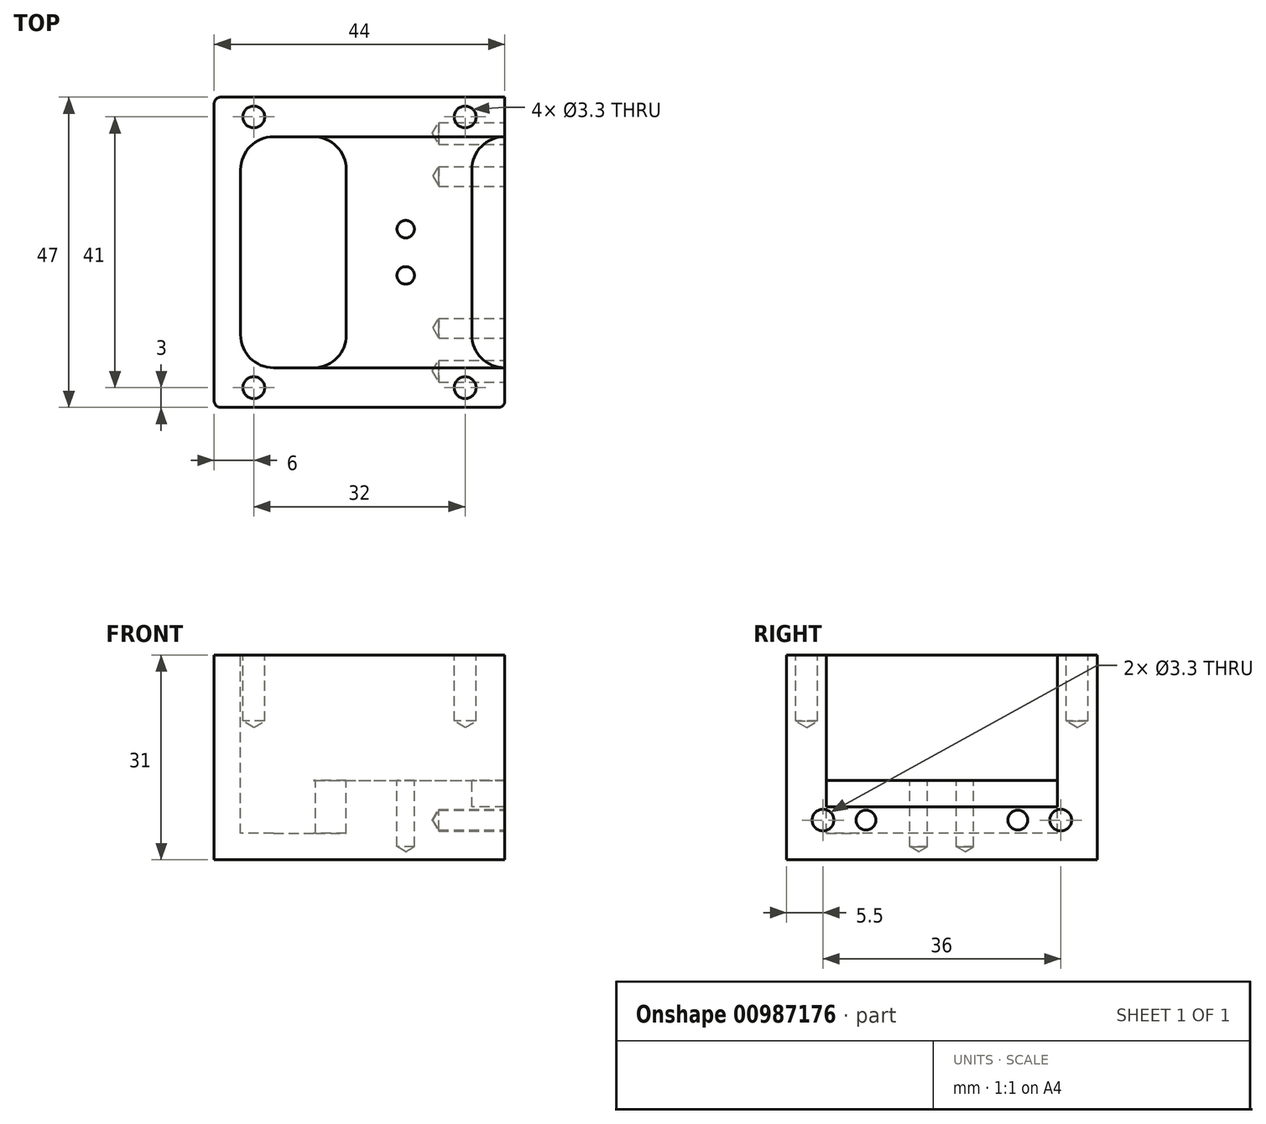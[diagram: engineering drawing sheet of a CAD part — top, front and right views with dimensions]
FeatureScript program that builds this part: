
annotation { "Feature Type Name" : "Feature", "Feature Type Description" : "" }
export const myFeature = defineFeature(function(context is Context, id is Id, definition is map)
    precondition{}
    {
        {
            var Q0;
            Q0=qCreatedBy(makeId("Top.planeOp"),FACE);
            var sketch = newSketch(context, id + "F0", { "sketchPlane" : qUnion([Q0])});
            skLineSegment(sketch, "E0", {"start": v(0, -28.75) * mm, "end": v(-27, -28.75) * mm});
            skLineSegment(sketch, "E1.bottom", {"start": v(-27, -28.75) * mm, "end": v(17, -28.75) * mm});
            skLineSegment(sketch, "E1.top", {"start": v(-27, 18.25) * mm, "end": v(17, 18.25) * mm});
            skLineSegment(sketch, "E1.left", {"start": v(-27, -28.75) * mm, "end": v(-27, 18.25) * mm});
            skLineSegment(sketch, "E1.right", {"start": v(17, -28.75) * mm, "end": v(17, 18.25) * mm});
            skSolve(sketch);
        }
        {
            var Q0;
            Q0=makeQuery(id+"F0.imprint","IMPRINT",FACE,{"disambiguationData":[TD([[makeQuery(id+"F0.imprint","IMPRINT",EDGE,{"derivedFrom":sQuery(id+"F0.wireOp",EDGE,"E1.top")}),-1.0]])]});
            extrude(context, id + "F1", {"entities" : qUnion([Q0]), "depth" : 31 * mm, "offsetDistance" : 25 * mm});
        }
        {
            var Q0;
            Q0=makeQuery(id+"F1.opExtrude","CAP_FACE",FACE,{"disambiguationData":[OSD([sQuery(id+"F0.wireOp",EDGE,"E1.bottom"),sQuery(id+"F0.wireOp",EDGE,"E1.top"),sQuery(id+"F0.wireOp",EDGE,"E1.left"),sQuery(id+"F0.wireOp",EDGE,"E1.right")])],"isStart":false});
            var sketch = newSketch(context, id + "F2", { "sketchPlane" : qUnion([Q0])});
            skLineSegment(sketch, "E2.right", {"start": v(17, 12.25) * mm, "end": v(17, -22.75) * mm});
            skPoint(sketch, "E3.visualSharp", {"position": v(-23, 12.25) * mm});
            skPoint(sketch, "E4.visualSharp", {"position": v(-23, -22.75) * mm});
            skLineSegment(sketch, "E5.bottom", {"start": v(-18, 12.25) * mm, "end": v(17, 12.25) * mm});
            skLineSegment(sketch, "E5.top", {"start": v(-18, -22.75) * mm, "end": v(17, -22.75) * mm});
            skLineSegment(sketch, "E5.left", {"start": v(-23, 7.25) * mm, "end": v(-23, -17.75) * mm});
            skArc(sketch, "E6.filletArc", {"start": v(-18, 12.25) * mm, "mid": v(-21.54, 10.79) * mm, "end": v(-23, 7.25) * mm});
            skArc(sketch, "E7.filletArc", {"start": v(-23, -17.75) * mm, "mid": v(-21.54, -21.29) * mm, "end": v(-18, -22.75) * mm});
            skSolve(sketch);
        }
        {
            var Q0;
            Q0 = qSketchRegion(id + "F2", true);
            extrude(context, id + "F3", {"entities" : qUnion([Q0]), "operationType" : NewBodyOperationType.REMOVE, "oppositeDirection" : true, "depth" : 19 * mm, "offsetDistance" : 25 * mm});
        }
        {
            var Q0;
            Q0=makeQuery(id+"F3.boolean.opBoolean","COPY",FACE,{"derivedFrom":makeQuery(id+"F3.opExtrude","CAP_FACE",FACE,{"disambiguationData":[OSD([sQuery(id+"F2.wireOp",EDGE,"E5.bottom"),sQuery(id+"F2.wireOp",EDGE,"E5.top"),sQuery(id+"F2.wireOp",EDGE,"E5.left"),sQuery(id+"F2.wireOp",EDGE,"E2.right"),sQuery(id+"F2.wireOp",EDGE,"E6.filletArc"),sQuery(id+"F2.wireOp",EDGE,"E7.filletArc")])],"isStart":false})});
            var sketch = newSketch(context, id + "F4", { "sketchPlane" : qUnion([Q0])});
            skLineSegment(sketch, "E8", {"start": v(-7, -5.25) * mm, "end": v(-7, 12.25) * mm});
            skLineSegment(sketch, "E9", {"start": v(-7, 7.25) * mm, "end": v(-7, -22.75) * mm});
            skLineSegment(sketch, "E10.bottom", {"start": v(-12, 12.25) * mm, "end": v(-18, 12.25) * mm});
            skLineSegment(sketch, "E10.top", {"start": v(-12, -22.76) * mm, "end": v(-18, -22.76) * mm});
            skLineSegment(sketch, "E10.left", {"start": v(-7, 12.25) * mm, "end": v(-7, -17.76) * mm});
            skLineSegment(sketch, "E10.right", {"start": v(-23, 7.25) * mm, "end": v(-23, -17.76) * mm});
            skPoint(sketch, "E11.visualSharp", {"position": v(-23, 12.25) * mm});
            skArc(sketch, "E11.filletArc", {"start": v(-18, 12.25) * mm, "mid": v(-21.54, 10.79) * mm, "end": v(-23, 7.25) * mm});
            skPoint(sketch, "E12.visualSharp", {"position": v(-23, -22.76) * mm});
            skArc(sketch, "E12.filletArc", {"start": v(-23, -17.76) * mm, "mid": v(-21.54, -21.3) * mm, "end": v(-18, -22.76) * mm});
            skPoint(sketch, "E13.visualSharp", {"position": v(-7, -22.76) * mm});
            skArc(sketch, "E13.filletArc", {"start": v(-12, -22.76) * mm, "mid": v(-8.46, -21.3) * mm, "end": v(-7, -17.76) * mm});
            skPoint(sketch, "E14.visualSharp", {"position": v(-7, 12.25) * mm});
            skArc(sketch, "E14.filletArc", {"start": v(-7, 7.25) * mm, "mid": v(-8.46, 10.79) * mm, "end": v(-12, 12.25) * mm});
            skSolve(sketch);
        }
        {
            var Q0;
            Q0=makeQuery(id+"F4.imprint","IMPRINT",FACE,{"disambiguationData":[TD([[makeQuery(id+"F4.imprint","IMPRINT",EDGE,{"derivedFrom":sQuery(id+"F4.wireOp",EDGE,"E10.bottom")}),-1.0]])]});
            extrude(context, id + "F5", {"entities" : qUnion([Q0]), "operationType" : NewBodyOperationType.REMOVE, "oppositeDirection" : true, "depth" : (27 - 19) * mm, "offsetDistance" : 25 * mm});
        }
        {
            var Q0;
            Q0=makeQuery(id+"F3.boolean.opBoolean","COPY",FACE,{"derivedFrom":makeQuery(id+"F3.opExtrude","CAP_FACE",FACE,{"disambiguationData":[OSD([sQuery(id+"F2.wireOp",EDGE,"E5.bottom"),sQuery(id+"F2.wireOp",EDGE,"E5.top"),sQuery(id+"F2.wireOp",EDGE,"E5.left"),sQuery(id+"F2.wireOp",EDGE,"E2.right"),sQuery(id+"F2.wireOp",EDGE,"E6.filletArc"),sQuery(id+"F2.wireOp",EDGE,"E7.filletArc")])],"isStart":false})});
            var sketch = newSketch(context, id + "F6", { "sketchPlane" : qUnion([Q0])});
            skLineSegment(sketch, "E15.bottom", {"start": v(17, 12.25) * mm, "end": v(17, 12.25) * mm});
            skLineSegment(sketch, "E15.top", {"start": v(17, -22.75) * mm, "end": v(17, -22.75) * mm});
            skLineSegment(sketch, "E15.left", {"start": v(17, 12.25) * mm, "end": v(17, -22.75) * mm});
            skLineSegment(sketch, "E15.right", {"start": v(12, 7.25) * mm, "end": v(12, -17.75) * mm});
            skPoint(sketch, "E16.visualSharp", {"position": v(12, 12.25) * mm});
            skArc(sketch, "E16.filletArc", {"start": v(17, 12.25) * mm, "mid": v(13.46, 10.79) * mm, "end": v(12, 7.25) * mm});
            skPoint(sketch, "E17.visualSharp", {"position": v(12, -22.75) * mm});
            skArc(sketch, "E17.filletArc", {"start": v(12, -17.75) * mm, "mid": v(13.46, -21.29) * mm, "end": v(17, -22.75) * mm});
            skSolve(sketch);
        }
        {
            var Q0;
            Q0=makeQuery(id+"F1.opExtrude","CAP_FACE",FACE,{"disambiguationData":[OSD([sQuery(id+"F0.wireOp",EDGE,"E1.bottom"),sQuery(id+"F0.wireOp",EDGE,"E1.top"),sQuery(id+"F0.wireOp",EDGE,"E1.left"),sQuery(id+"F0.wireOp",EDGE,"E1.right")])],"isStart":false});
            var sketch = newSketch(context, id + "F7", { "sketchPlane" : qUnion([Q0])});
            skLineSegment(sketch, "E18.bottom", {"start": v(-27, 18.25) * mm, "end": v(-21, 18.25) * mm});
            skLineSegment(sketch, "E18.top", {"start": v(-27, 15.25) * mm, "end": v(-21, 15.25) * mm});
            skLineSegment(sketch, "E18.left", {"start": v(-27, 18.25) * mm, "end": v(-27, 15.25) * mm});
            skLineSegment(sketch, "E18.right", {"start": v(-21, 18.25) * mm, "end": v(-21, 15.25) * mm});
            skLineSegment(sketch, "E19.MirrorCS", {"start": v(-27, -25.75) * mm, "end": v(-21, -25.75) * mm});
            skLineSegment(sketch, "E20.MirrorCS", {"start": v(-27, -28.75) * mm, "end": v(-21, -28.75) * mm});
            skLineSegment(sketch, "E21.MirrorCS", {"start": v(-27, -28.75) * mm, "end": v(-27, -25.75) * mm});
            skLineSegment(sketch, "E22.MirrorCS", {"start": v(-21, -28.75) * mm, "end": v(-21, -25.75) * mm});
            skLineSegment(sketch, "E23.MirrorCS", {"start": v(17, 18.25) * mm, "end": v(11, 18.25) * mm});
            skLineSegment(sketch, "E24.MirrorCS", {"start": v(11, 18.25) * mm, "end": v(11, 15.25) * mm});
            skLineSegment(sketch, "E25.MirrorCS", {"start": v(17, 15.25) * mm, "end": v(11, 15.25) * mm});
            skLineSegment(sketch, "E26.MirrorCS", {"start": v(17, 18.25) * mm, "end": v(17, 15.25) * mm});
            skLineSegment(sketch, "E27.MirrorCS", {"start": v(17, -28.75) * mm, "end": v(17, -25.75) * mm});
            skLineSegment(sketch, "E28.MirrorCS", {"start": v(17, -25.75) * mm, "end": v(11, -25.75) * mm});
            skLineSegment(sketch, "E29.MirrorCS", {"start": v(11, -28.75) * mm, "end": v(11, -25.75) * mm});
            skLineSegment(sketch, "E30.MirrorCS", {"start": v(17, -28.75) * mm, "end": v(11, -28.75) * mm});
            skSolve(sketch);
        }
        {
            var Q0;
            Q0=sQuery(id+"F7.wireOp",VERTEX,"E18.top.end");
            var Q1;
            Q1=sQuery(id+"F7.wireOp",VERTEX,"E19.MirrorCS.end");
            var Q2;
            Q2=sQuery(id+"F7.wireOp",VERTEX,"E28.MirrorCS.end");
            var Q3;
            Q3=sQuery(id+"F7.wireOp",VERTEX,"E24.MirrorCS.end");
            var Q4;
            Q4=makeQuery(id+"F1.opExtrude","SWEPT_BODY",BODY,{"disambiguationData":[OSD([sQuery(id+"F0.wireOp",EDGE,"E1.bottom"),sQuery(id+"F0.wireOp",EDGE,"E1.top"),sQuery(id+"F0.wireOp",EDGE,"E1.left"),sQuery(id+"F0.wireOp",EDGE,"E1.right")])]});
            hole(context, id + "F8", {"style" : HoleStyle.SIMPLE, "endStyle" : HoleEndStyle.BLIND, "standardTappedOrClearance" : lookupTablePath({ "standard" : "ISO", "engagement" : "75%", "pitch" : "0.7 mm", "size" : "M4", "type" : "Tapped" }), "standardBlindInLast" : lookupTablePath({ "standard" : "ISO", "fit" : "Normal", "engagement" : "75%", "pitch" : "0.7 mm", "size" : "M4", "type" : "Clearance & tapped" }), "holeDiameter" : 3.3 * mm, "majorDiameter" : 4 * mm, "showTappedDepth" : true, "holeDepth" : 10 * mm, "isTappedThrough" : true, "tappedDepth" : 10 * mm, "tapClearance" : 0, "locations" : qUnion([Q0, Q1, Q2, Q3]), "scope" : qUnion([Q4])});
        }
        {
            var Q0;
            Q0=makeQuery(id+"F6.imprint","IMPRINT",FACE,{"disambiguationData":[TD([[makeQuery(id+"F6.imprint","IMPRINT",EDGE,{"derivedFrom":sQuery(id+"F6.wireOp",EDGE,"E15.left")}),1.0]])]});
            extrude(context, id + "F9", {"entities" : qUnion([Q0]), "operationType" : NewBodyOperationType.REMOVE, "oppositeDirection" : true, "depth" : 4 * mm, "offsetDistance" : 25 * mm});
        }
        {
            var Q0;
            Q0=makeQuery(id+"F3.boolean.opBoolean","COPY",FACE,{"derivedFrom":makeQuery(id+"F3.opExtrude","CAP_FACE",FACE,{"disambiguationData":[OSD([sQuery(id+"F2.wireOp",EDGE,"E5.bottom"),sQuery(id+"F2.wireOp",EDGE,"E5.top"),sQuery(id+"F2.wireOp",EDGE,"E5.left"),sQuery(id+"F2.wireOp",EDGE,"E2.right"),sQuery(id+"F2.wireOp",EDGE,"E6.filletArc"),sQuery(id+"F2.wireOp",EDGE,"E7.filletArc")])],"isStart":false})});
            var sketch = newSketch(context, id + "F10", { "sketchPlane" : qUnion([Q0])});
            skLineSegment(sketch, "E31.0", {"start": v(-27, 18.25) * mm, "end": v(17, 18.25) * mm});
            skLineSegment(sketch, "E32", {"start": v(12, -5.25) * mm, "end": v(12, 18.25) * mm});
            skLineSegment(sketch, "E33.bottom", {"start": v(12, 18.25) * mm, "end": v(2, 18.25) * mm});
            skLineSegment(sketch, "E33.top", {"start": v(12, -1.75) * mm, "end": v(2, -1.75) * mm});
            skLineSegment(sketch, "E33.left", {"start": v(12, 18.25) * mm, "end": v(12, -1.75) * mm});
            skLineSegment(sketch, "E33.right", {"start": v(2, 18.25) * mm, "end": v(2, -1.75) * mm});
            skLineSegment(sketch, "E34.MirrorCS", {"start": v(2, -28.75) * mm, "end": v(2, -8.75) * mm});
            skLineSegment(sketch, "E35.MirrorCS", {"start": v(12, -8.75) * mm, "end": v(2, -8.75) * mm});
            skSolve(sketch);
        }
        {
            var Q0;
            Q0=sQuery(id+"F10.wireOp",VERTEX,"E33.top.end");
            var Q1;
            Q1=sQuery(id+"F10.wireOp",VERTEX,"E34.MirrorCS.end");
            var Q2;
            Q2=makeQuery(id+"F1.opExtrude","SWEPT_BODY",BODY,{"disambiguationData":[OSD([sQuery(id+"F0.wireOp",EDGE,"E1.bottom"),sQuery(id+"F0.wireOp",EDGE,"E1.top"),sQuery(id+"F0.wireOp",EDGE,"E1.left"),sQuery(id+"F0.wireOp",EDGE,"E1.right")])]});
            hole(context, id + "F11", {"style" : HoleStyle.SIMPLE, "endStyle" : HoleEndStyle.BLIND, "standardTappedOrClearance" : lookupTablePath({ "standard" : "ISO", "engagement" : "75%", "pitch" : "0.35 mm", "size" : "M3", "type" : "Tapped" }), "standardBlindInLast" : lookupTablePath({ "standard" : "ISO", "fit" : "Normal", "engagement" : "75%", "pitch" : "0.35 mm", "size" : "M3", "type" : "Clearance & tapped" }), "holeDiameter" : 2.65 * mm, "majorDiameter" : 3 * mm, "showTappedDepth" : true, "holeDepth" : 10 * mm, "isTappedThrough" : true, "tappedDepth" : 10 * mm, "tapClearance" : 0, "locations" : qUnion([Q0, Q1]), "scope" : qUnion([Q2])});
        }
        {
            var Q0;
            Q0=makeQuery(id+"F1.opExtrude","SWEPT_FACE",FACE,{"disambiguationData":[OSD([sQuery(id+"F0.wireOp",EDGE,"E1.right")])]});
            var sketch = newSketch(context, id + "F12", { "sketchPlane" : qUnion([Q0])});
            skPoint(sketch, "E36", {"position": v(-23.25, 6) * mm});
            skPoint(sketch, "E37", {"position": v(-16.75, 6) * mm});
            skLineSegment(sketch, "E38", {"start": v(-5.25, 0) * mm, "end": v(-5.25, 8) * mm});
            skPoint(sketch, "E39.MirrorP", {"position": v(6.25, 6) * mm});
            skPoint(sketch, "E40.MirrorP", {"position": v(12.75, 6) * mm});
            skSolve(sketch);
        }
        {
            var Q0;
            Q0=sQuery(id+"F12.wireOp",VERTEX,"E37");
            var Q1;
            Q1=sQuery(id+"F12.wireOp",VERTEX,"E39.MirrorP");
            var Q2;
            Q2=makeQuery(id+"F1.opExtrude","SWEPT_BODY",BODY,{"disambiguationData":[OSD([sQuery(id+"F0.wireOp",EDGE,"E1.bottom"),sQuery(id+"F0.wireOp",EDGE,"E1.top"),sQuery(id+"F0.wireOp",EDGE,"E1.left"),sQuery(id+"F0.wireOp",EDGE,"E1.right")])]});
            hole(context, id + "F13", {"style" : HoleStyle.SIMPLE, "endStyle" : HoleEndStyle.BLIND, "standardTappedOrClearance" : lookupTablePath({ "standard" : "ISO", "size" : "3", "type" : "Drilled" }), "standardBlindInLast" : lookupTablePath({ "standard" : "ISO", "size" : "3", "type" : "Drilled" }), "holeDiameter" : 3 * mm, "majorDiameter" : 3 * mm, "holeDepth" : 10 * mm, "isTappedThrough" : true, "tappedDepth" : 10 * mm, "tapClearance" : 0, "locations" : qUnion([Q0, Q1]), "scope" : qUnion([Q2])});
        }
        {
            var Q0;
            Q0=sQuery(id+"F12.wireOp",VERTEX,"E40.MirrorP");
            var Q1;
            Q1=sQuery(id+"F12.wireOp",VERTEX,"E36");
            var Q2;
            Q2=makeQuery(id+"F1.opExtrude","SWEPT_BODY",BODY,{"disambiguationData":[OSD([sQuery(id+"F0.wireOp",EDGE,"E1.bottom"),sQuery(id+"F0.wireOp",EDGE,"E1.top"),sQuery(id+"F0.wireOp",EDGE,"E1.left"),sQuery(id+"F0.wireOp",EDGE,"E1.right")])]});
            hole(context, id + "F14", {"style" : HoleStyle.SIMPLE, "endStyle" : HoleEndStyle.BLIND, "standardTappedOrClearance" : lookupTablePath({ "standard" : "ISO", "engagement" : "75%", "pitch" : "0.7 mm", "size" : "M4", "type" : "Tapped" }), "standardBlindInLast" : lookupTablePath({ "standard" : "ISO", "fit" : "Normal", "engagement" : "75%", "pitch" : "0.7 mm", "size" : "M4", "type" : "Clearance & tapped" }), "holeDiameter" : 3.3 * mm, "majorDiameter" : 4 * mm, "showTappedDepth" : true, "holeDepth" : 10 * mm, "isTappedThrough" : true, "tappedDepth" : 10 * mm, "tapClearance" : 0, "locations" : qUnion([Q0, Q1]), "scope" : qUnion([Q2])});
        }
        {
            var Q0;
            Q0=makeQuery(id+"F1.opExtrude","SWEPT_EDGE",EDGE,{"disambiguationData":[OSD([sQuery(id+"F0.wireOp",EDGE,"E1.bottom"),sQuery(id+"F0.wireOp",EDGE,"E1.left")])]});
            var Q1;
            Q1=makeQuery(id+"F1.opExtrude","SWEPT_EDGE",EDGE,{"disambiguationData":[OSD([sQuery(id+"F0.wireOp",EDGE,"E1.top"),sQuery(id+"F0.wireOp",EDGE,"E1.left")])]});
            fillet(context, id + "F15", {"entities" : qUnion([Q0, Q1]), "radius" : 1 * mm, "tangentPropagation" : true, "allowEdgeOverflow" : false});
        }
    });
